# Revit family: Gira_211400
name_source: partatom
category: Elektroinstallationen
revit_build: Autodesk Revit 2017 (Build: 20160225_1515(x64)
units: mm (PartAtom-declared; Revit-internal decimal feet)

## family parameters
Basisbauteil = Fläche
Beim Laden mit Abzugskörper schneiden = Nein
Bemaßung runder Anschluss = Durchmesser verwenden
Beschriftungsausrichtung beibehalten = Nein
Gemeinsam genutzt = Nein
Raumberechnungspunkt = Nein
Teiletyp = Normal

## types (1)
- Heizungsaktor Basic 6f KNX REG
    Andere Bussysteme = ohne
    Anzahl der Ausgänge = 0
    Anzahl der binären Eingänge = 0
    BIM = https://media.stage.bim.site 8f.rfa
    BIMSITE_PRODUCT_ID = a8b0bfac80ab459d18165d86efc775a7bda54a18
    Beschreibung = KNX Heizungsaktor Basic 6fach  REG plus Merkmale:  Heizungsaktor zum Schalten elektrothermischer Stellantriebe für Heizungen oder Kühldecken.  Ansteuerung über 1 Bit- oder 1 Byte-Stellgrößentelegramme.  Bei 1 Byte-Stellgrößen werden die Ausgänge durch eine Pulsweitenmodulation (PWM) angesteuert.  Stellantriebe mit Charakteristik stromlos geöffnet" oder "stromlos geschlossen" ansteuerbar.  Stellantriebe mit Nennspannung 24 V oder 230 V ansteuerbar.  Überlastsicher, kurzschlusssicher.  Standardschutz.  Rückmeldung über Bus z. B. bei Überlast und Kurzschluss.  Schalten der Heizkreispumpe (Standardfunktionen).  Passive Sammelrückmeldung der angeschlossenen Stellantriebe.  Hinweise :  An allen Ausgängen müssen Ventile mit der gleichen Betriebsspannung angeschlossen werden.  VDE-Zulassung gemäß EN 60669-1, EN 60669-2-1.  Montage auf DIN-Hutschiene."
    Blindleistung = Nein
    Breite in Teilungseinheiten = 4
    Busspannung pufferbar = Nein
    Bussystem Funkbus = Nein
    Bussystem KNX = Ja
    Bussystem KNX-Funk = Nein
    Bussystem LON = Nein
    Bussystem Powernet = Nein
    Datenblatt = https://media.stage.bim.site
    Datenblatt 1 = https://media.stage.bim.site
    GTIN = 4010337018414
    Geeignet für C-Last = Nein
    HAN = 211400
    Handschaltung = Nein
    HeinzeBIM = https://www.heinze.de
    Hersteller = Gira
    Kosten = 0 $
    Max. Anzahl der Schaltausgänge = 0
    Mit Busankopplung = Nein
    Mit LED-Anzeige = Nein
    Modulare Erweiterungsmöglichkeit = Nein
    Montageart = REG
    Produktseite = https://media.stage.bim.site
    Schutzart (IP) = IP20
    Stellgröße schaltend = Ja
    Stellgröße stetig = Nein
    Tarifumschaltung = Nein
    Typname = Heizungsaktor Basic 6f KNX REG
    URL = https://www.gira.de
    Ventilschutzfunktion = Nein
    Verschiedene Phasen anschließbar = Nein
    Vor Ort-/Handbedienung = Nein
    Vorgabe-Ansicht = 1219 mm
    Zulassung nach PTB = Nein

## geometry (parser evidence)
native form markers: Sweep x3
no freeform markers — native parametric forms only
